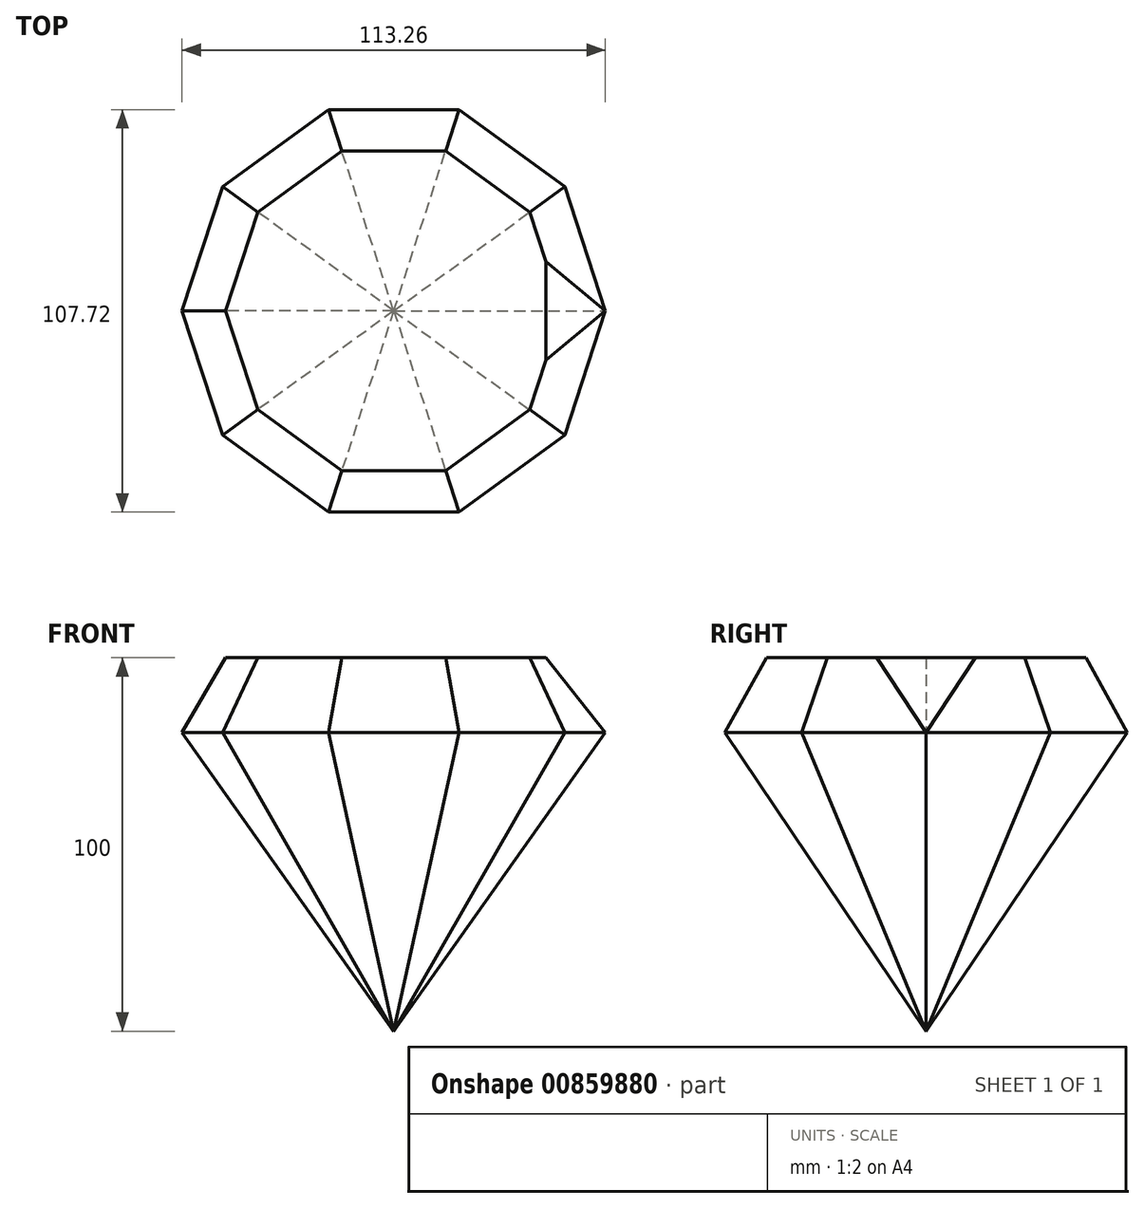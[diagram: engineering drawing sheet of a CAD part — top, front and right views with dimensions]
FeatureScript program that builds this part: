
annotation { "Feature Type Name" : "Feature", "Feature Type Description" : "" }
export const myFeature = defineFeature(function(context is Context, id is Id, definition is map)
    precondition{}
    {
        {
            var Q0;
            Q0=qCreatedBy(makeId("Top.planeOp"),FACE);
            cPlane(context, id + "F0", {"entities" : qUnion([Q0]), "cplaneType" : CPlaneType.OFFSET, "offset" : 80 * mm, "width" : 150 * mm, "height" : 150 * mm});
        }
        {
            var Q0;
            Q0=qCreatedBy(id+"F0.planeOp",FACE);
            var sketch = newSketch(context, id + "F1", { "sketchPlane" : qUnion([Q0])});
            skCircle(sketch, "E0.cCircle", {"center": v(0, 0) * mm, "radius": 53.86 * mm, "construction": true});
            skLineSegment(sketch, "E0.0", {"start": v(56.63, 0) * mm, "end": v(45.82, -33.29) * mm});
            skLineSegment(sketch, "E0.1", {"start": v(45.82, -33.29) * mm, "end": v(17.5, -53.86) * mm});
            skLineSegment(sketch, "E0.2", {"start": v(17.5, -53.86) * mm, "end": v(-17.5, -53.86) * mm});
            skLineSegment(sketch, "E0.3", {"start": v(-17.5, -53.86) * mm, "end": v(-45.82, -33.29) * mm});
            skLineSegment(sketch, "E0.4", {"start": v(-45.82, -33.29) * mm, "end": v(-56.63, 0) * mm});
            skLineSegment(sketch, "E0.5", {"start": v(-56.63, 0) * mm, "end": v(-45.82, 33.29) * mm});
            skLineSegment(sketch, "E0.6", {"start": v(-45.82, 33.29) * mm, "end": v(-17.5, 53.86) * mm});
            skLineSegment(sketch, "E0.7", {"start": v(-17.5, 53.86) * mm, "end": v(17.5, 53.86) * mm});
            skLineSegment(sketch, "E0.8", {"start": v(17.5, 53.86) * mm, "end": v(45.82, 33.29) * mm});
            skLineSegment(sketch, "E0.9", {"start": v(45.82, 33.29) * mm, "end": v(56.63, 0) * mm});
            skPoint(sketch, "E0.0.midPoint", {"position": v(51.22, -16.64) * mm});
            skSolve(sketch);
        }
        {
            var Q0;
            Q0=qCreatedBy(makeId("Top.planeOp"),FACE);
            var sketch = newSketch(context, id + "F2", { "sketchPlane" : qUnion([Q0])});
            skPoint(sketch, "E1", {"position": v(0, 0) * mm});
            skSolve(sketch);
        }
        {
            var Q0;
            Q0=sQuery(id+"F2.wireOp",VERTEX,"E1");
            var Q1;
            Q1=makeQuery(id+"F1.imprint","IMPRINT",FACE,{"disambiguationData":[TD([[makeQuery(id+"F1.imprint","IMPRINT",EDGE,{"derivedFrom":sQuery(id+"F1.wireOp",EDGE,"E0.0")}),-1.0]])]});
            loft(context, id + "F3", {"sheetProfilesArray" : [{ "sheetProfileEntities" : qUnion([Q0]) }, { "sheetProfileEntities" : qUnion([Q1]) }]});
        }
        {
            var Q0;
            Q0=makeQuery(id+"F3.opLoft","CAP_FACE",FACE,{"disambiguationData":[OSD([makeQuery(id+"F1.imprint","IMPRINT",FACE,{"disambiguationData":[TD([[makeQuery(id+"F1.imprint","IMPRINT",EDGE,{"derivedFrom":sQuery(id+"F1.wireOp",EDGE,"E0.0")}),-1.0]])]})])],"isStart":true});
            var sketch = newSketch(context, id + "F4", { "sketchPlane" : qUnion([Q0])});
            skLineSegment(sketch, "E2.0.0", {"start": v(56.63, 0) * mm, "end": v(45.82, 33.29) * mm});
            skLineSegment(sketch, "E2.0.1", {"start": v(45.82, 33.29) * mm, "end": v(17.5, 53.86) * mm});
            skLineSegment(sketch, "E2.0.2", {"start": v(17.5, 53.86) * mm, "end": v(-17.5, 53.86) * mm});
            skLineSegment(sketch, "E2.0.3", {"start": v(-17.5, 53.86) * mm, "end": v(-45.82, 33.29) * mm});
            skLineSegment(sketch, "E2.0.4", {"start": v(-45.82, 33.29) * mm, "end": v(-56.63, 0) * mm});
            skLineSegment(sketch, "E2.0.5", {"start": v(-56.63, 0) * mm, "end": v(-45.82, -33.29) * mm});
            skLineSegment(sketch, "E2.0.6", {"start": v(-45.82, -33.29) * mm, "end": v(-17.5, -53.86) * mm});
            skLineSegment(sketch, "E2.0.7", {"start": v(-17.5, -53.86) * mm, "end": v(17.5, -53.86) * mm});
            skLineSegment(sketch, "E2.0.8", {"start": v(17.5, -53.86) * mm, "end": v(45.82, -33.29) * mm});
            skLineSegment(sketch, "E2.0.9", {"start": v(45.82, -33.29) * mm, "end": v(56.63, 0) * mm});
            skSolve(sketch);
        }
        {
            var Q0;
            Q0 = qSketchRegion(id + "F4", true);
            extrude(context, id + "F5", {"entities" : qUnion([Q0]), "operationType" : NewBodyOperationType.ADD, "depth" : 20 * mm, "offsetDistance" : 25 * mm, "hasDraft" : true, "draftAngle" : 29 * degree, "draftPullDirection" : true});
        }
        {
            var Q0;
            Q0=makeQuery(id+"F5.opExtrude","CAP_FACE",FACE,{"disambiguationData":[OSD([sQuery(id+"F4.wireOp",EDGE,"E2.0.0"),sQuery(id+"F4.wireOp",EDGE,"E2.0.1"),sQuery(id+"F4.wireOp",EDGE,"E2.0.2"),sQuery(id+"F4.wireOp",EDGE,"E2.0.3"),sQuery(id+"F4.wireOp",EDGE,"E2.0.4"),sQuery(id+"F4.wireOp",EDGE,"E2.0.5"),sQuery(id+"F4.wireOp",EDGE,"E2.0.6"),sQuery(id+"F4.wireOp",EDGE,"E2.0.7"),sQuery(id+"F4.wireOp",EDGE,"E2.0.8"),sQuery(id+"F4.wireOp",EDGE,"E2.0.9")])],"isStart":false});
            var sketch = newSketch(context, id + "F6", { "sketchPlane" : qUnion([Q0])});
            skLineSegment(sketch, "E3", {"start": v(40.68, 13.22) * mm, "end": v(44.97, 0) * mm});
            skLineSegment(sketch, "E4", {"start": v(44.97, 0) * mm, "end": v(40.68, -13.22) * mm});
            skLineSegment(sketch, "E5", {"start": v(40.68, -13.22) * mm, "end": v(40.68, 13.22) * mm});
            skSolve(sketch);
        }
        {
            var Q0;
            Q0=qCreatedBy(id+"F0.planeOp",FACE);
            var sketch = newSketch(context, id + "F7", { "sketchPlane" : qUnion([Q0])});
            skPoint(sketch, "E6", {"position": v(56.63, 0) * mm});
            skSolve(sketch);
        }
        {
            var Q1;
            Q1=makeQuery(id+"F6.imprint","IMPRINT",FACE,{"disambiguationData":[TD([[makeQuery(id+"F6.imprint","IMPRINT",EDGE,{"derivedFrom":sQuery(id+"F6.wireOp",EDGE,"E3")}),1.0]])]});
            var Q2;
            Q2=sQuery(id+"F7.wireOp",VERTEX,"E6");
            loft(context, id + "F8", {"operationType" : NewBodyOperationType.REMOVE, "sheetProfilesArray" : [{ "sheetProfileEntities" : qUnion([Q1]) }, { "sheetProfileEntities" : qUnion([Q2]) }]});
        }
        {
            var Q0;
            Q0=qCreatedBy(makeId("Front.planeOp"),FACE);
            var sketch = newSketch(context, id + "F9", { "sketchPlane" : qUnion([Q0])});
            skLineSegment(sketch, "E7", {"start": v(0, 20.85) * mm, "end": v(0, 0) * mm, "construction": true});
            skSolve(sketch);
        }
    });
